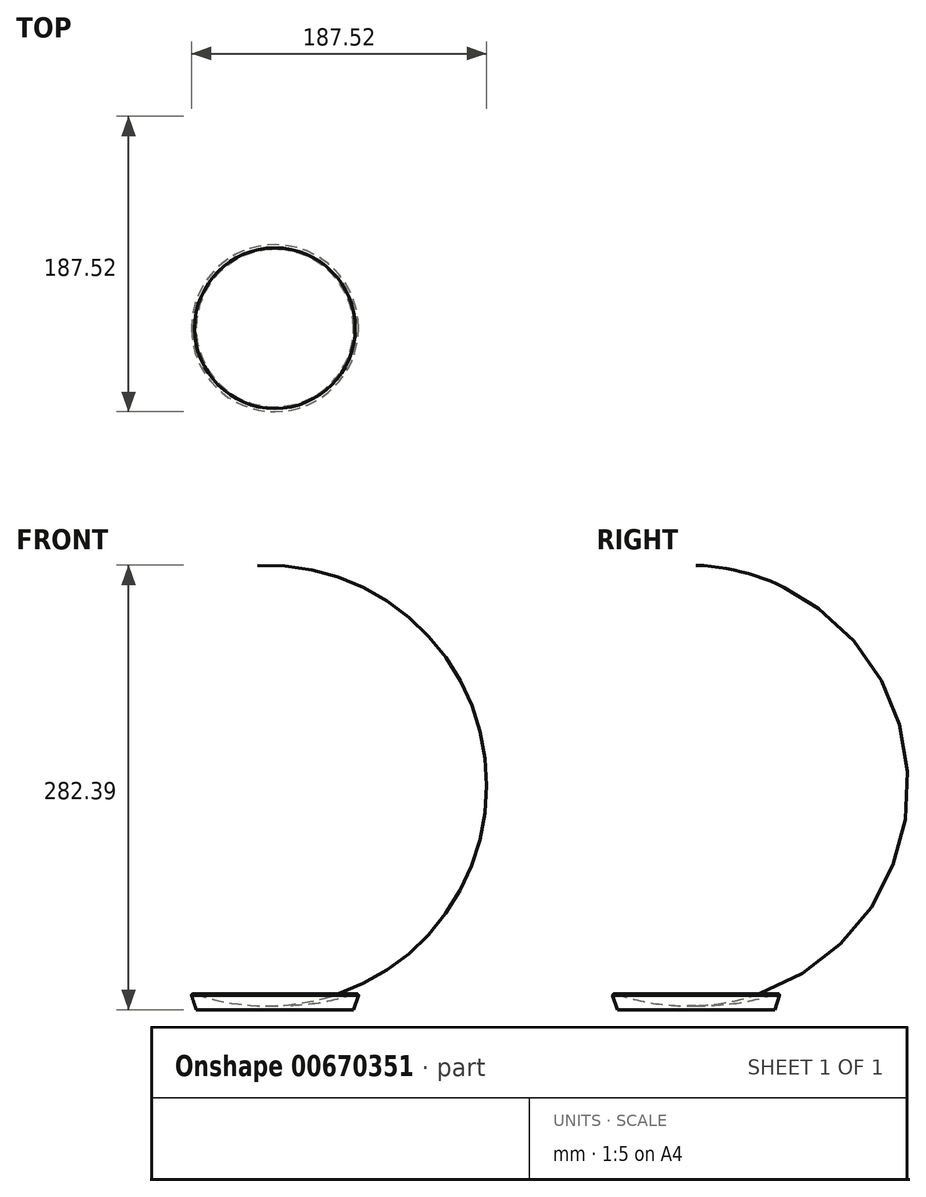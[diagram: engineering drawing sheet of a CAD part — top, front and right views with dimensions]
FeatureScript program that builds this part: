
annotation { "Feature Type Name" : "Feature", "Feature Type Description" : "" }
export const myFeature = defineFeature(function(context is Context, id is Id, definition is map)
    precondition{}
    {
        {
            var Q0;
            Q0=qCreatedBy(makeId("Front.planeOp"),FACE);
            var sketch = newSketch(context, id + "F0", { "sketchPlane" : qUnion([Q0])});
            skLineSegment(sketch, "E0", {"start": v(0, 0) * mm, "end": v(-53, 0) * mm});
            skLineSegment(sketch, "E1", {"start": v(-53, 0) * mm, "end": v(-53, 10) * mm});
            skLineSegment(sketch, "E2", {"start": v(0, 0) * mm, "end": v(0, 10) * mm, "construction": true});
            skLineSegment(sketch, "E3", {"start": v(-53, 10) * mm, "end": v(-51, 10) * mm});
            skArc(sketch, "E4", {"start": v(-51, 10) * mm, "mid": v(-25.85, 3.88) * mm, "end": v(0, 2.5) * mm});
            skLineSegment(sketch, "E5", {"start": v(0, 2.5) * mm, "end": v(0, 0) * mm});
            skSolve(sketch);
        }
        {
            var Q0;
            Q0=makeQuery(id+"F0.imprint","IMPRINT",FACE,{"disambiguationData":[TD([[makeQuery(id+"F0.imprint","IMPRINT",EDGE,{"derivedFrom":sQuery(id+"F0.wireOp",EDGE,"E0")}),-1.0]])]});
            var Q1;
            Q1=sQuery(id+"F0.wireOp",EDGE,"E2");
            revolve(context, id + "F1", {"entities" : qUnion([Q0]), "axis" : qUnion([Q1]), "revolveType" : RevolveType.FULL});
        }
        {
            var Q0;
            Q0=makeQuery(id+"F1.opRevolve","SWEPT_EDGE",EDGE,{"disambiguationData":[OSD([sQuery(id+"F0.wireOp",EDGE,"E0"),sQuery(id+"F0.wireOp",EDGE,"E1")])]});
            chamfer(context, id + "F2", {"entities" : qUnion([Q0]), "chamferType" : ChamferType.TWO_OFFSETS, "width1" : 3 * mm, "oppositeDirection" : false, "width2" : 9 * mm, "tangentPropagation" : true});
        }
        {
            var Q0;
            Q0=makeQuery(id+"F1.opRevolve","SWEPT_EDGE",EDGE,{"disambiguationData":[OSD([sQuery(id+"F0.wireOp",EDGE,"E1"),sQuery(id+"F0.wireOp",EDGE,"E3")])]});
            fillet(context, id + "F3", {"entities" : qUnion([Q0]), "radius" : 1 * mm, "tangentPropagation" : true, "allowEdgeOverflow" : false});
        }
    });
